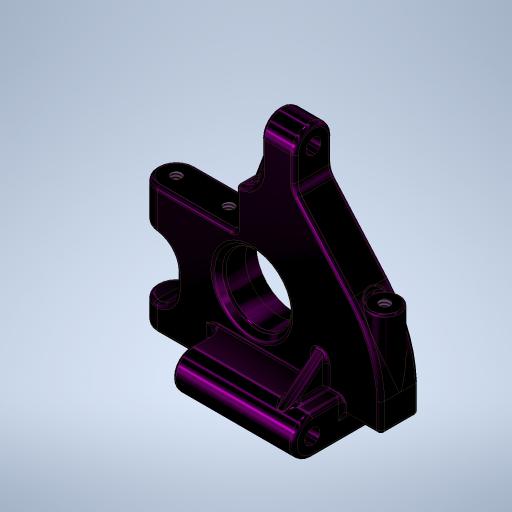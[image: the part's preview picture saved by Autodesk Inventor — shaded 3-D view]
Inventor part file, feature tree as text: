
AUTODESK INVENTOR PART (.ipt)
format: ipt  version: 2023.1 (Build 271208000, 208)  size: 1,035,264 bytes
history: native  units: in
note: dims shown in document units (in); Inventor stores cm internally (conversion verified against a paired STEP export)
features: fillet x22, sketch x19, extrude x13, plane x8, hole x4, projected_geometry x4, other x2, rib x2, chamfer x1
ambient origin geometry x8: Origin, YZ Plane, XZ Plane, XY Plane, X Axis, Y Axis, Z Axis, Center Point
bodies: Solid1 (feature_tree)
feature tree (75):
  extrude  "Extrusion1"  Depth=1.05in
  extrude  "Extrusion2"  Depth=0.315in
  fillet  "Fillet1"  Radius=0.5in
  extrude  "Extrusion3"  TaperAngle=120.0deg  [1 undecoded]
  extrude  "Extrusion4"  Depth=0.989in
  extrude  "Extrusion5"  Depth=0.3356in
  extrude  "Extrusion6"  Depth=1.0in
  extrude  "Extrusion7"  Depth=0.315in
  fillet  "Fillet2"  Radius=0.1875in
  extrude  "Extrusion8"  Depth=0.1575in
  chamfer  "Chamfer1"  Distance=0.315in
  fillet  "Fillet3"  Radius=0.315in
  fillet  "Fillet4"  Radius=0.315in
  fillet  "Fillet5"  Radius=0.75in
  fillet  "Fillet6"  Radius=1.0625in
  fillet  "Fillet7"  Radius=0.6825in
  fillet  "Fillet8"  Radius=0.035in
  fillet  "Fillet9"  Radius=0.625in
  fillet  "Fillet10"  Radius=0.1288in
  other  "Work Point1"
  plane  "Work Plane1"
  other  "Work Axis1"
  plane  "Work Plane5"
  extrude  "Extrusion9"  Depth=0.55in
  fillet  "Fillet11"  [1 undecoded]
  fillet  "Fillet12"  Radius=0.1875in
  fillet  "Fillet13"  Radius=0.032in
  fillet  "Fillet14"  Radius=0.032in
  fillet  "Fillet15"  Radius=0.032in
  fillet  "Fillet16"  Radius=0.125in
  hole  "Hole1"  [1 undecoded]
  plane  "Work Plane6"
  rib  "Rib1"
  fillet  "Fillet17"  Radius=0.032in
  fillet  "Fillet18"  [1 undecoded]
  plane  "Work Plane7"
  extrude  "Extrusion10"  [1 undecoded]
  extrude  "Extrusion11"  Depth=0.315in
  fillet  "Fillet19"  Radius=0.1288in
  hole  "Hole2"  [1 undecoded]
  plane  "Work Plane8"
  rib  "Rib2"
  fillet  "Fillet20"  Radius=0.032in
  fillet  "Fillet21"  Radius=0.032in
  extrude  "Extrusion12"  Depth=0.015in
  extrude  "Extrusion13"  [1 undecoded]
  fillet  "Fillet22"  Radius=0.1in
  hole  "Hole3"  [1 undecoded]
  hole  "Hole4"  [1 undecoded]
  sketch  "Sketch1"  dims[d0=2.0in d1=1.05in]
  sketch  "Sketch2"  dims[d3=0.215in d4=0.315in d5=0.5in]
  sketch  "Sketch3"  dims[d6=0.361in d8=120.0deg]
  sketch  "Sketch4"  dims[d9=0.2762in d10=0.989in]
  sketch  "Sketch5"  dims[d11=1.825in d12=0.3356in]
  sketch  "Sketch6"  dims[d13=0.425in d14=1.0in]
  sketch  "Sketch7"  dims[d15=0.315in d16=0.0in d17=0.315in d18=0.1875in]
  sketch  "Sketch8"  dims[d19=0.315in d20=0.0in d21=0.1575in]
  plane  "Work Plane2"
  plane  "Work Plane3"
  plane  "Work Plane4"
  sketch  "Sketch9"  dims[d22=0.3438in d23=0.315in d24=0.0in d25=0.315in d26=0.0in d27=0.315in d28=0.0in d29=0.75in d30=1.0625in d31=0.6825in d32=0.035in d33=0.0in d34=0.625in d35=0.1288in d36=0.0in]
  sketch  "Sketch10"  dims[d37=0.032in d38=0.55in d39=0.0in d40=0.0in]
  sketch  "Sketch11"  dims[d41=0.05in d42=0.125in d43=45.0deg d44=0.1875in d45=0.032in d46=0.032in d47=0.032in d48=0.125in]
  sketch  "Sketch12"  dims[d49=0.032in d50=0.015in d51=0.032in d52=0.0in]
  sketch  "Sketch13"  dims[d53=0.25in d54=-0.1575in]
  sketch  "Sketch14"  dims[d55=-1.0in d56=0.315in d57=0.1288in d58=0.0in]
  sketch  "Sketch15"  dims[d59=0.032in d60=0.125in d61=0.032in d62=0.032in]
  sketch  "Sketch16"  dims[d63=0.032in d64=0.015in]
  sketch  "Sketch17"  dims[d65=0.125in d66=0.224in d67=0.375in d68=0.25in d69=0.5635in d70=0.349in d71=0.8108in d72=-0.5in d73=0.1in]
  sketch  "Sketch18"  dims[d74=0.1in d75=0.0in d76=0.0in d77=0.1in d78=0.1in d79=0.032in]
  sketch  "Sketch19"  dims[d80=0.032in d81=-1.0in d82=0.25in d83=0.1288in d84=0.0in d85=0.1288in d86=0.0in d87=0.015in d88=0.0849in d89=0.224in d90=0.375in d91=0.25in d92=0.5635in d93=0.315in d94=0.8108in d95=0.1in d96=0.1in d97=0.0in d98=0.0in d99=0.1in d100=0.1in d101=0.032in d102=0.032in d103=0.22in d104=0.1288in d105=0.0in d106=0.15in d107=0.0in d108=0.015in d109=0.125in d110=0.224in d111=0.375in d112=0.25in d113=0.5635in d114=0.315in d115=0.8108in d116=0.435in d117=0.0849in d118=0.224in d119=0.375in d120=0.25in d121=0.5635in d122=0.349in d123=0.8108in]
  projected_geometry  "Project Cut Edges1"
  projected_geometry  "Project Cut Edges2"
  projected_geometry  "Project Cut Edges3"
  projected_geometry  "Project Cut Edges4"
note: 9 required parameter values undecoded (feature->parameter linkage not recoverable at this tier; creation-order binding heuristic only, values carry confidence <= 0.55)
